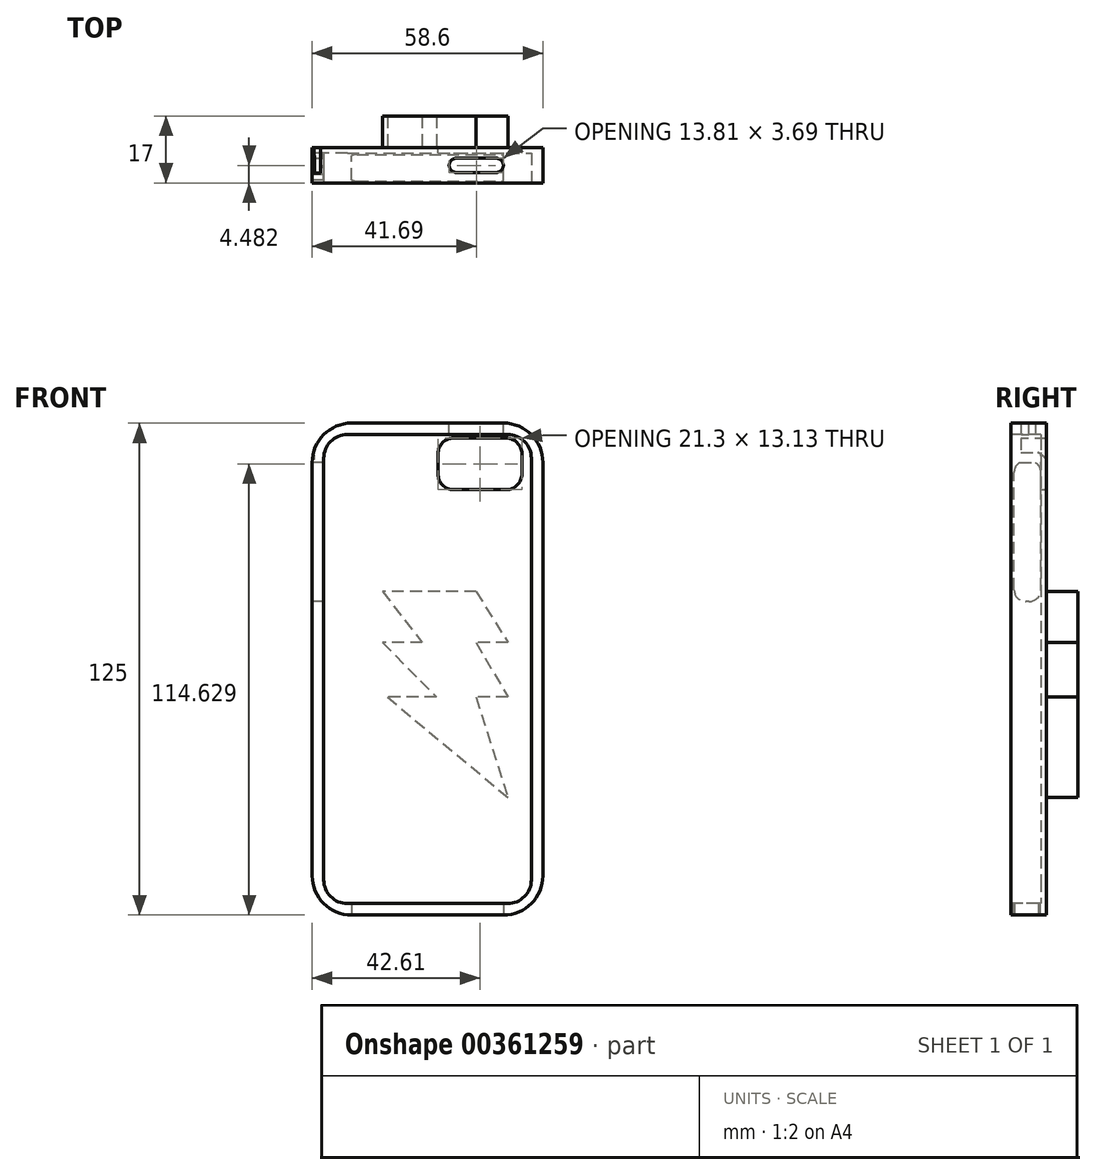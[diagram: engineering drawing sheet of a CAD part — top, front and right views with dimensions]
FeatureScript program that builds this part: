
annotation { "Feature Type Name" : "Feature", "Feature Type Description" : "" }
export const myFeature = defineFeature(function(context is Context, id is Id, definition is map)
    precondition{}
    {
        {
            var Q0;
            Q0=qCreatedBy(makeId("Front.planeOp"),FACE);
            var sketch = newSketch(context, id + "F0", { "sketchPlane" : qUnion([Q0])});
            skLineSegment(sketch, "E0.bottom", {"start": v(-24.63, 55.77) * mm, "end": v(13.97, 55.77) * mm});
            skLineSegment(sketch, "E0.top", {"start": v(-24.63, -69.23) * mm, "end": v(13.97, -69.23) * mm});
            skLineSegment(sketch, "E0.left", {"start": v(-34.63, 45.77) * mm, "end": v(-34.63, -59.23) * mm});
            skLineSegment(sketch, "E0.right", {"start": v(23.97, 45.77) * mm, "end": v(23.97, -59.23) * mm});
            skPoint(sketch, "E1.visualSharp", {"position": v(-34.63, 55.77) * mm});
            skArc(sketch, "E1.filletArc", {"start": v(-24.63, 55.77) * mm, "mid": v(-31.7, 52.85) * mm, "end": v(-34.63, 45.77) * mm});
            skPoint(sketch, "E2.visualSharp", {"position": v(23.97, 55.77) * mm});
            skArc(sketch, "E2.filletArc", {"start": v(23.97, 45.77) * mm, "mid": v(21.04, 52.85) * mm, "end": v(13.97, 55.77) * mm});
            skPoint(sketch, "E3.visualSharp", {"position": v(-34.63, -69.23) * mm});
            skArc(sketch, "E3.filletArc", {"start": v(-34.63, -59.23) * mm, "mid": v(-31.7, -66.3) * mm, "end": v(-24.63, -69.23) * mm});
            skPoint(sketch, "E4.visualSharp", {"position": v(23.97, -69.23) * mm});
            skArc(sketch, "E4.filletArc", {"start": v(13.97, -69.23) * mm, "mid": v(21.04, -66.3) * mm, "end": v(23.97, -59.23) * mm});
            skSolve(sketch);
        }
        {
            var Q0;
            Q0=makeQuery(id+"F0.imprint","IMPRINT",FACE,{"disambiguationData":[TD([[makeQuery(id+"F0.imprint","IMPRINT",EDGE,{"derivedFrom":sQuery(id+"F0.wireOp",EDGE,"E0.bottom")}),-1.0]])]});
            extrude(context, id + "F1", {"entities" : qUnion([Q0]), "depth" : 9 * mm});
        }
        {
            var Q0;
            Q0=makeQuery(id+"F1.opExtrude","SWEPT_FACE",FACE,{"disambiguationData":[OSD([sQuery(id+"F0.wireOp",EDGE,"E0.left")])]});
            var sketch = newSketch(context, id + "F2", { "sketchPlane" : qUnion([Q0])});
            skLineSegment(sketch, "E5.bottom", {"start": v(4.45, 10.4) * mm, "end": v(5.24, 10.4) * mm});
            skLineSegment(sketch, "E5.top", {"start": v(4.45, 46.25) * mm, "end": v(5.24, 46.25) * mm});
            skLineSegment(sketch, "E5.left", {"start": v(1.45, 13.4) * mm, "end": v(1.45, 43.25) * mm});
            skLineSegment(sketch, "E5.right", {"start": v(8.24, 13.4) * mm, "end": v(8.24, 43.25) * mm});
            skPoint(sketch, "E6.visualSharp", {"position": v(1.45, 46.25) * mm});
            skArc(sketch, "E6.filletArc", {"start": v(4.45, 46.25) * mm, "mid": v(2.32, 45.37) * mm, "end": v(1.45, 43.25) * mm});
            skPoint(sketch, "E7.visualSharp", {"position": v(1.45, 10.4) * mm});
            skArc(sketch, "E7.filletArc", {"start": v(1.45, 13.4) * mm, "mid": v(2.32, 11.29) * mm, "end": v(4.45, 10.4) * mm});
            skPoint(sketch, "E8.visualSharp", {"position": v(8.24, 46.25) * mm});
            skArc(sketch, "E8.filletArc", {"start": v(8.24, 43.25) * mm, "mid": v(7.36, 45.37) * mm, "end": v(5.24, 46.25) * mm});
            skPoint(sketch, "E9.visualSharp", {"position": v(8.24, 10.4) * mm});
            skArc(sketch, "E9.filletArc", {"start": v(5.24, 10.4) * mm, "mid": v(7.36, 11.29) * mm, "end": v(8.24, 13.4) * mm});
            skSolve(sketch);
        }
        {
            var Q0;
            Q0=makeQuery(id+"F2.imprint","IMPRINT",FACE,{"disambiguationData":[TD([[makeQuery(id+"F2.imprint","IMPRINT",EDGE,{"derivedFrom":sQuery(id+"F2.wireOp",EDGE,"E5.bottom")}),1.0]])]});
            extrude(context, id + "F3", {"entities" : qUnion([Q0]), "operationType" : NewBodyOperationType.REMOVE, "oppositeDirection" : true, "depth" : 5 * mm});
        }
        {
            var Q0;
            Q0=makeQuery(id+"F1.opExtrude","SWEPT_FACE",FACE,{"disambiguationData":[OSD([sQuery(id+"F0.wireOp",EDGE,"E0.top")])]});
            var sketch = newSketch(context, id + "F4", { "sketchPlane" : qUnion([Q0])});
            skPoint(sketch, "E10", {"position": v(-5.33, 9) * mm});
            skLineSegment(sketch, "E11.bottom", {"start": v(-23.28, 8.53) * mm, "end": v(13.6, 8.53) * mm});
            skLineSegment(sketch, "E11.top", {"start": v(-23.28, 1.74) * mm, "end": v(13.6, 1.74) * mm});
            skLineSegment(sketch, "E11.left", {"start": v(-26.28, 5.53) * mm, "end": v(-26.28, 4.74) * mm});
            skLineSegment(sketch, "E11.right", {"start": v(16.6, 5.53) * mm, "end": v(16.6, 4.74) * mm});
            skPoint(sketch, "E12.visualSharp", {"position": v(-26.28, 8.53) * mm});
            skArc(sketch, "E12.filletArc", {"start": v(-23.28, 8.53) * mm, "mid": v(-25.4, 7.65) * mm, "end": v(-26.28, 5.53) * mm});
            skPoint(sketch, "E13.visualSharp", {"position": v(-26.28, 1.74) * mm});
            skArc(sketch, "E13.filletArc", {"start": v(-26.28, 4.74) * mm, "mid": v(-25.4, 2.62) * mm, "end": v(-23.28, 1.74) * mm});
            skPoint(sketch, "E14.visualSharp", {"position": v(16.6, 1.74) * mm});
            skArc(sketch, "E14.filletArc", {"start": v(13.6, 1.74) * mm, "mid": v(15.72, 2.62) * mm, "end": v(16.6, 4.74) * mm});
            skPoint(sketch, "E15.visualSharp", {"position": v(16.6, 8.53) * mm});
            skArc(sketch, "E15.filletArc", {"start": v(16.6, 5.53) * mm, "mid": v(15.72, 7.65) * mm, "end": v(13.6, 8.53) * mm});
            skSolve(sketch);
        }
        {
            var Q0;
            Q0=makeQuery(id+"F4.imprint","IMPRINT",FACE,{"disambiguationData":[TD([[makeQuery(id+"F4.imprint","IMPRINT",EDGE,{"derivedFrom":sQuery(id+"F4.wireOp",EDGE,"E11.bottom")}),-1.0]])]});
            extrude(context, id + "F5", {"entities" : qUnion([Q0]), "operationType" : NewBodyOperationType.REMOVE, "oppositeDirection" : true, "depth" : 5.53 * mm});
        }
        {
            var Q0;
            Q0=makeQuery(id+"F1.opExtrude","CAP_FACE",FACE,{"disambiguationData":[OSD([sQuery(id+"F0.wireOp",EDGE,"E0.bottom"),sQuery(id+"F0.wireOp",EDGE,"E0.top"),sQuery(id+"F0.wireOp",EDGE,"E0.left"),sQuery(id+"F0.wireOp",EDGE,"E0.right"),sQuery(id+"F0.wireOp",EDGE,"E1.filletArc"),sQuery(id+"F0.wireOp",EDGE,"E2.filletArc"),sQuery(id+"F0.wireOp",EDGE,"E3.filletArc"),sQuery(id+"F0.wireOp",EDGE,"E4.filletArc")])],"isStart":false});
            var sketch = newSketch(context, id + "F6", { "sketchPlane" : qUnion([Q0])});
            skLineSegment(sketch, "E16.bottom", {"start": v(-25.7, 52.85) * mm, "end": v(15.04, 52.85) * mm});
            skLineSegment(sketch, "E16.top", {"start": v(-25.7, -66.3) * mm, "end": v(15.04, -66.3) * mm});
            skLineSegment(sketch, "E16.left", {"start": v(-31.7, 46.85) * mm, "end": v(-31.7, -60.3) * mm});
            skLineSegment(sketch, "E16.right", {"start": v(21.04, 46.85) * mm, "end": v(21.04, -60.3) * mm});
            skPoint(sketch, "E17.visualSharp", {"position": v(-31.7, 52.85) * mm});
            skArc(sketch, "E17.filletArc", {"start": v(-25.7, 52.85) * mm, "mid": v(-29.94, 51.09) * mm, "end": v(-31.7, 46.85) * mm});
            skPoint(sketch, "E18.visualSharp", {"position": v(21.04, 52.85) * mm});
            skArc(sketch, "E18.filletArc", {"start": v(21.04, 46.85) * mm, "mid": v(19.28, 51.09) * mm, "end": v(15.04, 52.85) * mm});
            skPoint(sketch, "E19.visualSharp", {"position": v(-31.7, -66.3) * mm});
            skArc(sketch, "E19.filletArc", {"start": v(-31.7, -60.3) * mm, "mid": v(-29.94, -64.54) * mm, "end": v(-25.7, -66.3) * mm});
            skPoint(sketch, "E20.visualSharp", {"position": v(21.04, -66.3) * mm});
            skArc(sketch, "E20.filletArc", {"start": v(15.04, -66.3) * mm, "mid": v(19.28, -64.54) * mm, "end": v(21.04, -60.3) * mm});
            skSolve(sketch);
        }
        {
            var Q0;
            Q0 = qSketchRegion(id + "F6", true);
            extrude(context, id + "F7", {"entities" : qUnion([Q0]), "operationType" : NewBodyOperationType.REMOVE, "oppositeDirection" : true, "depth" : 7.6 * mm});
        }
        {
            var Q0;
            Q0=makeQuery(id+"F1.opExtrude","SWEPT_FACE",FACE,{"disambiguationData":[OSD([sQuery(id+"F0.wireOp",EDGE,"E0.bottom")])]});
            var sketch = newSketch(context, id + "F8", { "sketchPlane" : qUnion([Q0])});
            skLineSegment(sketch, "E21.bottom", {"start": v(11.97, -6.36) * mm, "end": v(2.15, -6.36) * mm});
            skLineSegment(sketch, "E21.top", {"start": v(11.97, -2.67) * mm, "end": v(2.15, -2.67) * mm});
            skLineSegment(sketch, "E21.left", {"start": v(13.97, -4.67) * mm, "end": v(13.97, -4.36) * mm});
            skLineSegment(sketch, "E21.right", {"start": v(0.15, -4.67) * mm, "end": v(0.15, -4.36) * mm});
            skPoint(sketch, "E22.visualSharp", {"position": v(13.97, -6.36) * mm});
            skArc(sketch, "E22.filletArc", {"start": v(11.97, -6.36) * mm, "mid": v(13.38, -5.78) * mm, "end": v(13.97, -4.36) * mm});
            skPoint(sketch, "E23.visualSharp", {"position": v(13.97, -2.67) * mm});
            skArc(sketch, "E23.filletArc", {"start": v(13.97, -4.67) * mm, "mid": v(13.38, -3.26) * mm, "end": v(11.97, -2.67) * mm});
            skPoint(sketch, "E24.visualSharp", {"position": v(0.15, -6.36) * mm});
            skArc(sketch, "E24.filletArc", {"start": v(0.15, -4.36) * mm, "mid": v(0.74, -5.78) * mm, "end": v(2.15, -6.36) * mm});
            skPoint(sketch, "E25.visualSharp", {"position": v(0.15, -2.67) * mm});
            skArc(sketch, "E25.filletArc", {"start": v(2.15, -2.67) * mm, "mid": v(0.74, -3.26) * mm, "end": v(0.15, -4.67) * mm});
            skSolve(sketch);
        }
        {
            var Q0;
            {var subQ4=sQuery(id+"F8.wireOp",EDGE,"E21.bottom");Q0=makeQuery(id+"F8.imprint","IMPRINT",FACE,{"disambiguationData":[TD([[makeQuery(id+"F8.imprint","IMPRINT",EDGE,{"derivedFrom":subQ4}),-1.0]])]});}
            extrude(context, id + "F9", {"entities" : qUnion([Q0]), "operationType" : NewBodyOperationType.REMOVE, "oppositeDirection" : true, "depth" : 3 * mm});
        }
        {
            var Q0;
            Q0=makeQuery(id+"F1.opExtrude","CAP_FACE",FACE,{"disambiguationData":[OSD([sQuery(id+"F0.wireOp",EDGE,"E0.bottom"),sQuery(id+"F0.wireOp",EDGE,"E0.top"),sQuery(id+"F0.wireOp",EDGE,"E0.left"),sQuery(id+"F0.wireOp",EDGE,"E0.right"),sQuery(id+"F0.wireOp",EDGE,"E1.filletArc"),sQuery(id+"F0.wireOp",EDGE,"E2.filletArc"),sQuery(id+"F0.wireOp",EDGE,"E3.filletArc"),sQuery(id+"F0.wireOp",EDGE,"E4.filletArc")])],"isStart":true});
            var sketch = newSketch(context, id + "F10", { "sketchPlane" : qUnion([Q0])});
            skLineSegment(sketch, "E26.bottom", {"start": v(-14.63, 51.96) * mm, "end": v(-1.33, 51.96) * mm});
            skLineSegment(sketch, "E26.top", {"start": v(-14.63, 38.83) * mm, "end": v(-1.33, 38.83) * mm});
            skLineSegment(sketch, "E26.left", {"start": v(-18.63, 47.96) * mm, "end": v(-18.63, 42.83) * mm});
            skLineSegment(sketch, "E26.right", {"start": v(2.67, 47.96) * mm, "end": v(2.67, 42.83) * mm});
            skPoint(sketch, "E27.visualSharp", {"position": v(-18.63, 51.96) * mm});
            skArc(sketch, "E27.filletArc", {"start": v(-14.63, 51.96) * mm, "mid": v(-17.46, 50.8) * mm, "end": v(-18.63, 47.96) * mm});
            skPoint(sketch, "E28.visualSharp", {"position": v(-18.63, 38.83) * mm});
            skArc(sketch, "E28.filletArc", {"start": v(-18.63, 42.83) * mm, "mid": v(-17.46, 40) * mm, "end": v(-14.63, 38.83) * mm});
            skPoint(sketch, "E29.visualSharp", {"position": v(2.67, 38.83) * mm});
            skArc(sketch, "E29.filletArc", {"start": v(-1.33, 38.83) * mm, "mid": v(1.5, 40) * mm, "end": v(2.67, 42.83) * mm});
            skPoint(sketch, "E30.visualSharp", {"position": v(2.67, 51.96) * mm});
            skArc(sketch, "E30.filletArc", {"start": v(2.67, 47.96) * mm, "mid": v(1.5, 50.8) * mm, "end": v(-1.33, 51.96) * mm});
            skSolve(sketch);
        }
        {
            var Q0;
            Q0=makeQuery(id+"F10.imprint","IMPRINT",FACE,{"disambiguationData":[TD([[makeQuery(id+"F10.imprint","IMPRINT",EDGE,{"derivedFrom":sQuery(id+"F10.wireOp",EDGE,"E26.bottom")}),-1.0]])]});
            extrude(context, id + "F11", {"entities" : qUnion([Q0]), "operationType" : NewBodyOperationType.REMOVE, "oppositeDirection" : true, "depth" : 25 * mm});
        }
        {
            var Q0;
            Q0=makeQuery(id+"F4.imprint","IMPRINT",FACE,{"disambiguationData":[TD([[makeQuery(id+"F4.imprint","IMPRINT",EDGE,{"derivedFrom":sQuery(id+"F4.wireOp",EDGE,"E11.bottom")}),-1.0]])]});
            extrude(context, id + "F12", {"entities" : qUnion([Q0]), "operationType" : NewBodyOperationType.REMOVE, "oppositeDirection" : true, "depth" : 25 * mm});
        }
        {
            var Q0;
            Q0=makeQuery(id+"F1.opExtrude","CAP_FACE",FACE,{"disambiguationData":[OSD([sQuery(id+"F0.wireOp",EDGE,"E0.bottom"),sQuery(id+"F0.wireOp",EDGE,"E0.top"),sQuery(id+"F0.wireOp",EDGE,"E0.left"),sQuery(id+"F0.wireOp",EDGE,"E0.right"),sQuery(id+"F0.wireOp",EDGE,"E1.filletArc"),sQuery(id+"F0.wireOp",EDGE,"E2.filletArc"),sQuery(id+"F0.wireOp",EDGE,"E3.filletArc"),sQuery(id+"F0.wireOp",EDGE,"E4.filletArc")])],"isStart":true});
            var sketch = newSketch(context, id + "F13", { "sketchPlane" : qUnion([Q0])});
            skLineSegment(sketch, "E31", {"start": v(-7, 12.95) * mm, "end": v(16.76, 12.95) * mm});
            skLineSegment(sketch, "E32", {"start": v(16.76, 12.95) * mm, "end": v(6.7, 0) * mm});
            skLineSegment(sketch, "E33", {"start": v(6.7, 0) * mm, "end": v(16.76, 0) * mm});
            skLineSegment(sketch, "E34", {"start": v(16.76, 0) * mm, "end": v(3.05, -13.86) * mm});
            skLineSegment(sketch, "E35", {"start": v(3.05, -13.86) * mm, "end": v(15.54, -13.86) * mm});
            skLineSegment(sketch, "E36", {"start": v(15.54, -13.86) * mm, "end": v(-15.13, -39.36) * mm});
            skLineSegment(sketch, "E37", {"start": v(-7, 12.95) * mm, "end": v(-15.13, 0) * mm});
            skLineSegment(sketch, "E38", {"start": v(-15.13, 0) * mm, "end": v(-7, 0) * mm});
            skLineSegment(sketch, "E39", {"start": v(-7, 0) * mm, "end": v(-15.13, -13.86) * mm});
            skLineSegment(sketch, "E40", {"start": v(-15.13, -13.86) * mm, "end": v(-7, -13.86) * mm});
            skLineSegment(sketch, "E41", {"start": v(-7, -13.86) * mm, "end": v(-15.13, -39.36) * mm});
            skSolve(sketch);
        }
        {
            var Q0;
            Q0=makeQuery(id+"F13.imprint","IMPRINT",FACE,{"disambiguationData":[TD([[makeQuery(id+"F13.imprint","IMPRINT",EDGE,{"derivedFrom":sQuery(id+"F13.wireOp",EDGE,"E31")}),-1.0]])]});
            extrude(context, id + "F14", {"entities" : qUnion([Q0]), "operationType" : NewBodyOperationType.ADD, "depth" : 8 * mm});
        }
        {
            var Q0;
            Q0=makeQuery(id+"F1.opExtrude","CAP_FACE",FACE,{"disambiguationData":[OSD([sQuery(id+"F0.wireOp",EDGE,"E0.bottom"),sQuery(id+"F0.wireOp",EDGE,"E0.top"),sQuery(id+"F0.wireOp",EDGE,"E0.left"),sQuery(id+"F0.wireOp",EDGE,"E0.right"),sQuery(id+"F0.wireOp",EDGE,"E1.filletArc"),sQuery(id+"F0.wireOp",EDGE,"E2.filletArc"),sQuery(id+"F0.wireOp",EDGE,"E3.filletArc"),sQuery(id+"F0.wireOp",EDGE,"E4.filletArc")])],"isStart":true});
            var Q1;
            {var subQ2=sQuery(id+"F0.wireOp",EDGE,"E0.top");Q1=makeQuery(id+"F5.boolean.opBoolean","SPLIT",FACE,{"disambiguationData":[TD([makeQuery(id+"F5.opExtrude","SWEPT_FACE",FACE,{"disambiguationData":[OSD([sQuery(id+"F4.wireOp",EDGE,"E11.bottom")])]})])],"derivedFrom":makeQuery(id+"F1.opExtrude","SWEPT_FACE",FACE,{"disambiguationData":[OSD([subQ2])]})});}
            var Q2;
            Q2=makeQuery(id+"F1.opExtrude","SWEPT_FACE",FACE,{"disambiguationData":[OSD([sQuery(id+"F0.wireOp",EDGE,"E4.filletArc")])]});
            var Q3;
            {var subQ2=sQuery(id+"F0.wireOp",EDGE,"E0.top");Q3=makeQuery(id+"F5.boolean.opBoolean","SPLIT",FACE,{"disambiguationData":[TD([makeQuery(id+"F5.opExtrude","SWEPT_FACE",FACE,{"disambiguationData":[OSD([sQuery(id+"F4.wireOp",EDGE,"E11.top")])]})])],"derivedFrom":makeQuery(id+"F1.opExtrude","SWEPT_FACE",FACE,{"disambiguationData":[OSD([subQ2])]})});}
            var Q4;
            Q4=makeQuery(id+"F1.opExtrude","SWEPT_FACE",FACE,{"disambiguationData":[OSD([sQuery(id+"F0.wireOp",EDGE,"E1.filletArc")])]});
            shell(context, id + "F15", {"entities" : qUnion([Q0, Q1, Q2, Q3, Q4]), "thickness" : 2.5 * mm});
        }
    });
